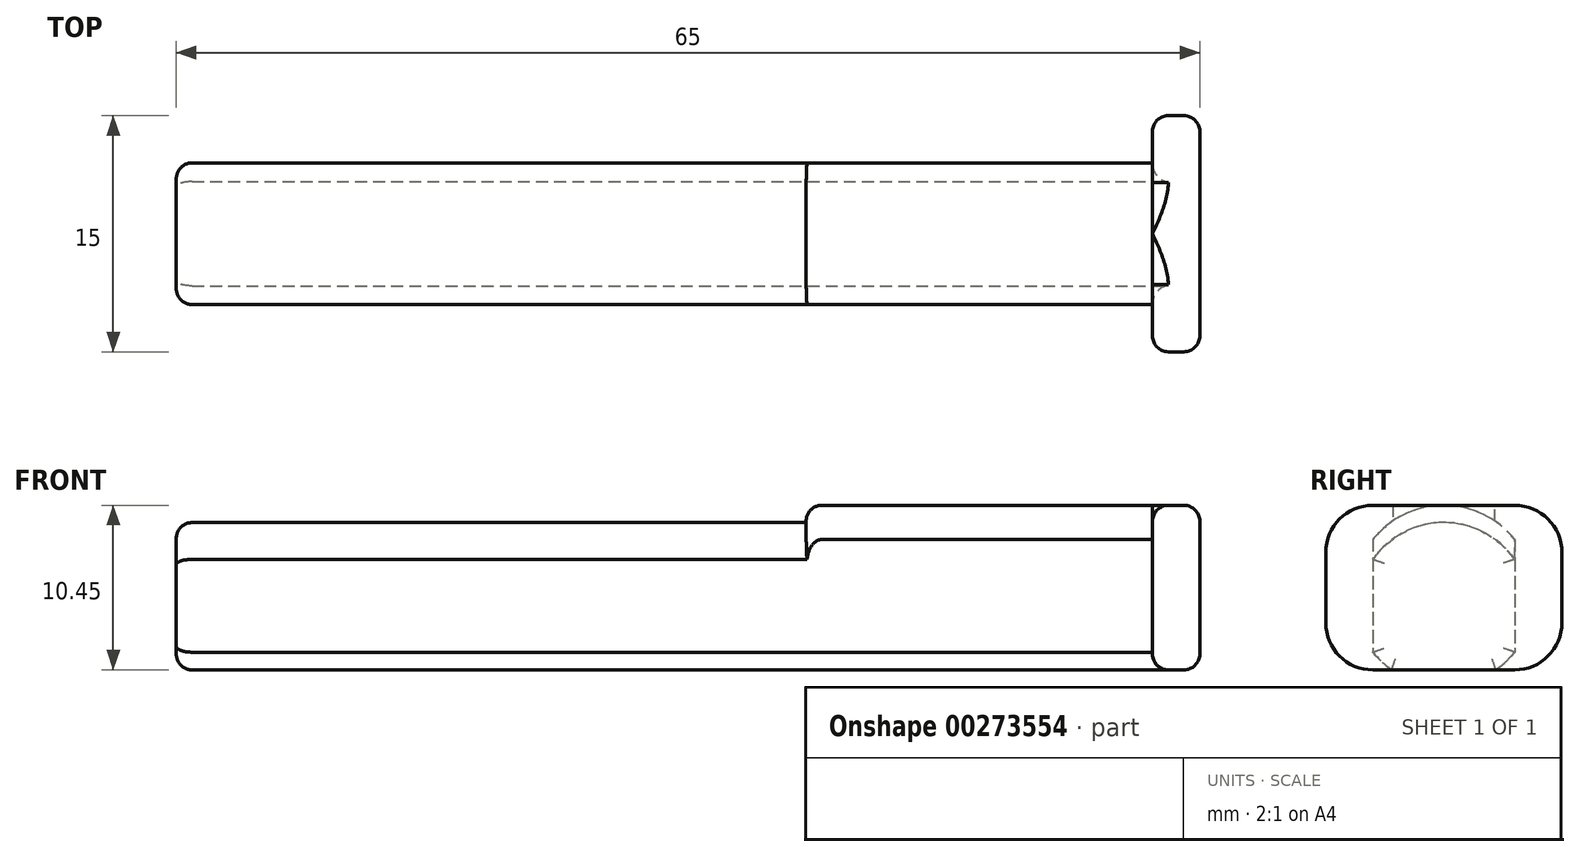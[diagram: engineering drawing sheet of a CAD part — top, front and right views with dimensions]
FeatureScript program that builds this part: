
annotation { "Feature Type Name" : "Feature", "Feature Type Description" : "" }
export const myFeature = defineFeature(function(context is Context, id is Id, definition is map)
    precondition{}
    {
        {
            var Q0;
            Q0=qCreatedBy(makeId("Right.planeOp"),FACE);
            var sketch = newSketch(context, id + "F0", { "sketchPlane" : qUnion([Q0])});
            skCircle(sketch, "E0", {"center": v(0, 0) * mm, "radius": 5.75 * mm});
            skCircle(sketch, "E1", {"center": v(0, -0.85) * mm, "radius": 5.5 * mm});
            skLineSegment(sketch, "E2.bottom", {"start": v(4.5, 10) * mm, "end": v(-4.5, 10) * mm});
            skLineSegment(sketch, "E2.top", {"start": v(4.5, -7.27) * mm, "end": v(-4.5, -7.27) * mm});
            skLineSegment(sketch, "E2.left", {"start": v(4.5, 10) * mm, "end": v(4.5, -7.27) * mm});
            skLineSegment(sketch, "E2.right", {"start": v(-4.5, 10) * mm, "end": v(-4.5, -7.27) * mm});
            skPoint(sketch, "E2.middle", {"position": v(0, 1.36) * mm});
            skLineSegment(sketch, "E3", {"start": v(-6.17, -4.7) * mm, "end": v(8.09, -4.7) * mm});
            skSolve(sketch);
        }
        {
            var Q0;
            {var subQ1=sQuery(id+"F0.wireOp",EDGE,"E0");var subQ7=sQuery(id+"F0.wireOp",EDGE,"E2.right");var subQ9=makeQuery(id+"F0.imprint","INTERSECT",VERTEX,{"disambiguationData":[OD(1.0)],"derivedFrom":[subQ1,subQ7]});Q0=makeQuery(id+"F0.imprint","IMPRINT",FACE,{"disambiguationData":[TD([[makeQuery(id+"F0.imprint","IMPRINT",EDGE,{"disambiguationData":[TD([[subQ9,-1.0]])],"derivedFrom":subQ1}),1.0]])]});}
            extrude(context, id + "F1", {"entities" : qUnion([Q0]), "oppositeDirection" : true, "depth" : 40 * mm});
        }
        {
            var Q0;
            {var subQ0=sQuery(id+"F0.wireOp",EDGE,"E2.right");var subQ1=sQuery(id+"F0.wireOp",EDGE,"E0");var subQ2=makeQuery(id+"F0.imprint","INTERSECT",VERTEX,{"disambiguationData":[OD(0.0)],"derivedFrom":[subQ1,subQ0]});Q0=makeQuery(id+"F0.imprint","IMPRINT",FACE,{"disambiguationData":[TD([[makeQuery(id+"F0.imprint","IMPRINT",EDGE,{"disambiguationData":[TD([[subQ2,1.0]])],"derivedFrom":subQ1}),1.0]])]});}
            var Q1;
            {var subQ1=sQuery(id+"F0.wireOp",EDGE,"E0");var subQ7=sQuery(id+"F0.wireOp",EDGE,"E2.right");var subQ9=makeQuery(id+"F0.imprint","INTERSECT",VERTEX,{"disambiguationData":[OD(1.0)],"derivedFrom":[subQ1,subQ7]});Q1=makeQuery(id+"F0.imprint","IMPRINT",FACE,{"disambiguationData":[TD([[makeQuery(id+"F0.imprint","IMPRINT",EDGE,{"disambiguationData":[TD([[subQ9,-1.0]])],"derivedFrom":subQ1}),1.0]])]});}
            extrude(context, id + "F2", {"entities" : qUnion([Q0, Q1]), "operationType" : NewBodyOperationType.ADD, "depth" : 22 * mm});
        }
        {
            var Q0;
            Q0=makeQuery(id+"F2.opExtrude","CAP_FACE",FACE,{"disambiguationData":[OSD([sQuery(id+"F0.wireOp",EDGE,"E0"),sQuery(id+"F0.wireOp",EDGE,"E2.left"),sQuery(id+"F0.wireOp",EDGE,"E2.right"),sQuery(id+"F0.wireOp",EDGE,"E3")])],"isStart":false});
            var sketch = newSketch(context, id + "F3", { "sketchPlane" : qUnion([Q0])});
            skLineSegment(sketch, "E4.bottom", {"start": v(7.5, -4.7) * mm, "end": v(-7.5, -4.7) * mm});
            skLineSegment(sketch, "E4.top", {"start": v(7.5, 5.75) * mm, "end": v(-7.5, 5.75) * mm});
            skLineSegment(sketch, "E4.left", {"start": v(7.5, -4.7) * mm, "end": v(7.5, 5.75) * mm});
            skLineSegment(sketch, "E4.right", {"start": v(-7.5, -4.7) * mm, "end": v(-7.5, 5.75) * mm});
            skPoint(sketch, "E4.middle", {"position": v(0, 0.52) * mm});
            skSolve(sketch);
        }
        {
            var Q0;
            Q0 = qSketchRegion(id + "F3", true);
            extrude(context, id + "F4", {"entities" : qUnion([Q0]), "operationType" : NewBodyOperationType.ADD, "depth" : 3 * mm});
        }
        {
            var Q0;
            Q0=makeQuery(id+"F4.opExtrude","SWEPT_EDGE",EDGE,{"disambiguationData":[OSD([sQuery(id+"F3.wireOp",EDGE,"E4.top"),sQuery(id+"F3.wireOp",EDGE,"E4.right")])]});
            var Q1;
            Q1=makeQuery(id+"F4.opExtrude","SWEPT_EDGE",EDGE,{"disambiguationData":[OSD([sQuery(id+"F3.wireOp",EDGE,"E4.bottom"),sQuery(id+"F3.wireOp",EDGE,"E4.right")])]});
            var Q2;
            Q2=makeQuery(id+"F4.opExtrude","SWEPT_EDGE",EDGE,{"disambiguationData":[OSD([sQuery(id+"F3.wireOp",EDGE,"E4.top"),sQuery(id+"F3.wireOp",EDGE,"E4.left")])]});
            var Q3;
            Q3=makeQuery(id+"F4.opExtrude","SWEPT_EDGE",EDGE,{"disambiguationData":[OSD([sQuery(id+"F3.wireOp",EDGE,"E4.bottom"),sQuery(id+"F3.wireOp",EDGE,"E4.left")])]});
            fillet(context, id + "F5", {"entities" : qUnion([Q0, Q1, Q2, Q3]), "radius" : 3 * mm, "tangentPropagation" : true, "allowEdgeOverflow" : false});
        }
        {
            var Q0;
            {var subQ0=sQuery(id+"F0.wireOp",EDGE,"E0");Q0=makeQuery(id+"F2.opExtrude","CAP_EDGE",EDGE,{"disambiguationData":[OSD([subQ0]),TDD([makeQuery(id+"F0.imprint","IMPRINT",EDGE,{"disambiguationData":[TD([[makeQuery(id+"F0.imprint","INTERSECT",VERTEX,{"disambiguationData":[OD(0.0)],"derivedFrom":[subQ0,sQuery(id+"F0.wireOp",EDGE,"E2.right")]}),1.0]])],"derivedFrom":subQ0})])],"isStart":true});}
            fillet(context, id + "F6", {"entities" : qUnion([Q0]), "radius" : 1 * mm, "tangentPropagation" : true, "allowEdgeOverflow" : false});
        }
        {
            var Q0;
            {var subQ0=sQuery(id+"F3.wireOp",EDGE,"E4.left");var subQ1=sQuery(id+"F3.wireOp",EDGE,"E4.top");Q0=makeQuery(id+"F5.opFillet","BLEND_EDGE",EDGE,{"blendedFrom":[makeQuery(id+"F4.opExtrude","SWEPT_EDGE",EDGE,{"disambiguationData":[OSD([subQ1,subQ0])]}),makeQuery(id+"F4.opExtrude","CAP_FACE",FACE,{"disambiguationData":[OSD([sQuery(id+"F3.wireOp",EDGE,"E4.bottom"),subQ1,subQ0,sQuery(id+"F3.wireOp",EDGE,"E4.right")])],"isStart":false})],"blendedInto":[makeQuery(id+"F4.opExtrude","CAP_FACE",FACE,{"disambiguationData":[OSD([sQuery(id+"F3.wireOp",EDGE,"E4.bottom"),subQ1,subQ0,sQuery(id+"F3.wireOp",EDGE,"E4.right")])],"isStart":false})]});}
            var Q1;
            {var subQ0=sQuery(id+"F3.wireOp",EDGE,"E4.bottom");var subQ2=sQuery(id+"F3.wireOp",EDGE,"E4.top");var subQ3=sQuery(id+"F0.wireOp",EDGE,"E2.left");var subQ6=sQuery(id+"F3.wireOp",EDGE,"E4.left");var subQ7=makeQuery(id+"F4.opExtrude","CAP_FACE",FACE,{"disambiguationData":[OSD([subQ0,subQ2,subQ6,sQuery(id+"F3.wireOp",EDGE,"E4.right")])],"isStart":true});Q1=makeQuery(id+"F5.opFillet","BLEND_EDGE",EDGE,{"blendedFrom":[makeQuery(id+"F4.opExtrude","SWEPT_EDGE",EDGE,{"disambiguationData":[OSD([subQ2,subQ6])]}),makeQuery(id+"F4.boolean.opBoolean","SPLIT",FACE,{"disambiguationData":[TD([makeQuery(id+"F1.opExtrude","SWEPT_FACE",FACE,{"disambiguationData":[OSD([subQ3])]})])],"derivedFrom":subQ7})],"blendedInto":[makeQuery(id+"F4.boolean.opBoolean","SPLIT",FACE,{"disambiguationData":[TD([makeQuery(id+"F1.opExtrude","SWEPT_FACE",FACE,{"disambiguationData":[OSD([subQ3])]})])],"derivedFrom":subQ7})]});}
            fillet(context, id + "F7", {"entities" : qUnion([Q0, Q1]), "radius" : 1 * mm, "tangentPropagation" : true, "allowEdgeOverflow" : false});
        }
        {
            var Q0;
            Q0=makeQuery(id+"F1.opExtrude","CAP_FACE",FACE,{"disambiguationData":[OSD([sQuery(id+"F0.wireOp",EDGE,"E0"),sQuery(id+"F0.wireOp",EDGE,"E1"),sQuery(id+"F0.wireOp",EDGE,"E2.left"),sQuery(id+"F0.wireOp",EDGE,"E2.right"),sQuery(id+"F0.wireOp",EDGE,"E3")])],"isStart":false});
            fillet(context, id + "F8", {"entities" : qUnion([Q0]), "radius" : 1 * mm, "tangentPropagation" : true, "allowEdgeOverflow" : false});
        }
    });
